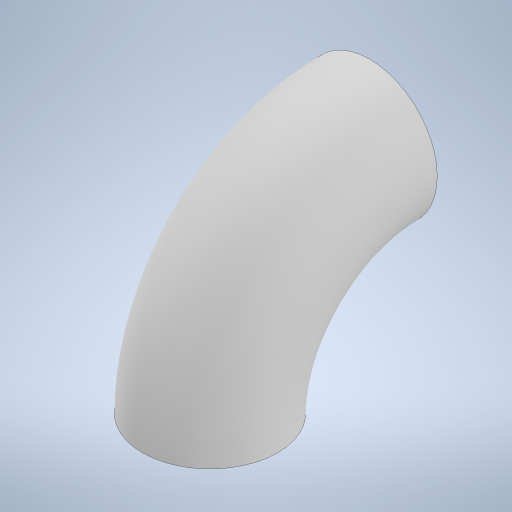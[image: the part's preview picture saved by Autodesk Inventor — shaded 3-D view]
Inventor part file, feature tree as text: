
AUTODESK INVENTOR PART (.ipt)
format: ipt  version: 2023 (Build 270158000, 158)  size: 266,240 bytes
history: native  units: mm
features: sketch x2, sweep x1
ambient origin geometry x8: Origin, YZ Plane, XZ Plane, XY Plane, X Axis, Y Axis, Z Axis, Center Point
bodies: Solido1 (feature_tree)
feature tree (3):
  sweep  "Sweep1"
  sketch  "Schizzo1"
  sketch  "Schizzo2"
